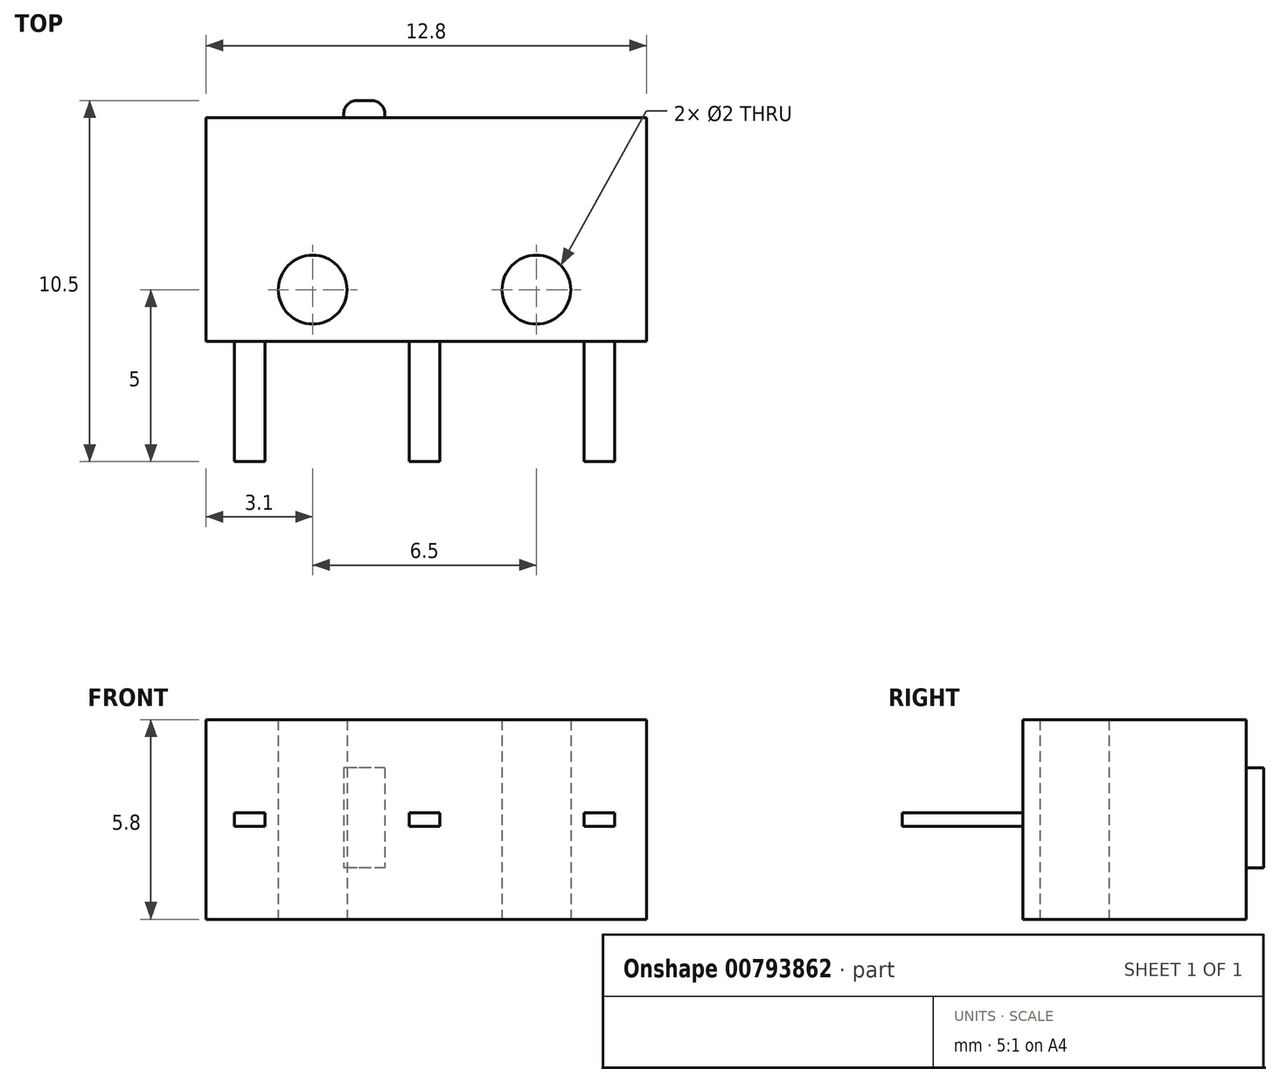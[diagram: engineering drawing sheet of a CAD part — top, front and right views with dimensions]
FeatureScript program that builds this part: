
annotation { "Feature Type Name" : "Feature", "Feature Type Description" : "" }
export const myFeature = defineFeature(function(context is Context, id is Id, definition is map)
    precondition{}
    {
        {
            var Q0;
            Q0=qCreatedBy(makeId("Top.planeOp"),FACE);
            var sketch = newSketch(context, id + "F0", { "sketchPlane" : qUnion([Q0])});
            skLineSegment(sketch, "E0.bottom", {"start": v(-6.35, 3.25) * mm, "end": v(6.45, 3.25) * mm});
            skLineSegment(sketch, "E0.top", {"start": v(-6.35, -3.25) * mm, "end": v(6.45, -3.25) * mm});
            skLineSegment(sketch, "E0.left", {"start": v(-6.35, 3.25) * mm, "end": v(-6.35, -3.25) * mm});
            skLineSegment(sketch, "E0.right", {"start": v(6.45, 3.25) * mm, "end": v(6.45, -3.25) * mm});
            skCircle(sketch, "E1", {"center": v(-3.25, -1.75) * mm, "radius": 1 * mm});
            skCircle(sketch, "E2", {"center": v(3.25, -1.75) * mm, "radius": 1 * mm});
            skSolve(sketch);
        }
        {
            var Q0;
            Q0=qSketchRegion(id+"F0",true);
            extrude(context, id + "F1", {"entities" : qUnion([Q0]), "depth" : 5.8 * mm, "offsetDistance" : 25 * mm});
        }
        {
            var Q0;
            Q0=makeQuery(id+"F1.opExtrude","SWEPT_FACE",FACE,{"disambiguationData":[OSD([sQuery(id+"F0.wireOp",EDGE,"E0.bottom")])]});
            var sketch = newSketch(context, id + "F2", { "sketchPlane" : qUnion([Q0])});
            skLineSegment(sketch, "E3.bottom", {"start": v(1.15, 4.4) * mm, "end": v(2.35, 4.4) * mm});
            skLineSegment(sketch, "E3.top", {"start": v(1.15, 1.5) * mm, "end": v(2.35, 1.5) * mm});
            skLineSegment(sketch, "E3.left", {"start": v(1.15, 4.4) * mm, "end": v(1.15, 1.5) * mm});
            skLineSegment(sketch, "E3.right", {"start": v(2.35, 4.4) * mm, "end": v(2.35, 1.5) * mm});
            skLineSegment(sketch, "E4", {"start": v(-3.25, 5.8) * mm, "end": v(-3.25, 0) * mm, "construction": true});
            skSolve(sketch);
        }
        {
            var Q0;
            Q0=qCreatedBy(makeId("Top.planeOp"),FACE);
            cPlane(context, id + "F3", {"entities" : qUnion([Q0]), "cplaneType" : CPlaneType.OFFSET, "offset" : 2.7 * mm, "width" : 150 * mm, "height" : 150 * mm});
        }
        {
            var Q0;
            Q0=qCreatedBy(id+"F3.planeOp",FACE);
            var sketch = newSketch(context, id + "F4", { "sketchPlane" : qUnion([Q0])});
            skLineSegment(sketch, "E5.bottom", {"start": v(-5.53, -3.25) * mm, "end": v(-4.63, -3.25) * mm});
            skLineSegment(sketch, "E5.top", {"start": v(-5.53, -6.75) * mm, "end": v(-4.63, -6.75) * mm});
            skLineSegment(sketch, "E5.left", {"start": v(-5.53, -3.25) * mm, "end": v(-5.53, -6.75) * mm});
            skLineSegment(sketch, "E5.right", {"start": v(-4.63, -3.25) * mm, "end": v(-4.63, -6.75) * mm});
            skLineSegment(sketch, "E6.bottom", {"start": v(-0.45, -3.25) * mm, "end": v(0.45, -3.25) * mm});
            skLineSegment(sketch, "E6.top", {"start": v(-0.45, -6.75) * mm, "end": v(0.45, -6.75) * mm});
            skLineSegment(sketch, "E6.left", {"start": v(-0.45, -3.25) * mm, "end": v(-0.45, -6.75) * mm});
            skLineSegment(sketch, "E6.right", {"start": v(0.45, -3.25) * mm, "end": v(0.45, -6.75) * mm});
            skLineSegment(sketch, "E7.bottom", {"start": v(4.63, -3.25) * mm, "end": v(5.53, -3.25) * mm});
            skLineSegment(sketch, "E7.top", {"start": v(4.63, -6.75) * mm, "end": v(5.53, -6.75) * mm});
            skLineSegment(sketch, "E7.left", {"start": v(4.63, -3.25) * mm, "end": v(4.63, -6.75) * mm});
            skLineSegment(sketch, "E7.right", {"start": v(5.53, -3.25) * mm, "end": v(5.53, -6.75) * mm});
            skPoint(sketch, "E8", {"position": v(-5.08, -6.75) * mm});
            skPoint(sketch, "E9", {"position": v(5.08, -6.75) * mm});
            skSolve(sketch);
        }
        {
            var Q0;
            Q0=qSketchRegion(id+"F4",true);
            extrude(context, id + "F5", {"entities" : qUnion([Q0]), "operationType" : NewBodyOperationType.ADD, "depth" : 0.4 * mm});
        }
        {
            var Q0;
            Q0=qSketchRegion(id+"F2",true);
            extrude(context, id + "F6", {"entities" : qUnion([Q0]), "operationType" : NewBodyOperationType.ADD, "depth" : .5 * mm});
        }
        {
            var Q0;
            Q0=makeQuery(id+"F6.opExtrude","CAP_EDGE",EDGE,{"disambiguationData":[OSD([sQuery(id+"F2.wireOp",EDGE,"E3.right")])],"isStart":false});
            var Q1;
            Q1=makeQuery(id+"F6.opExtrude","CAP_EDGE",EDGE,{"disambiguationData":[OSD([sQuery(id+"F2.wireOp",EDGE,"E3.left")])],"isStart":false});
            fillet(context, id + "F7", {"entities" : qUnion([Q0, Q1]), "radius" : .4 * mm, "tangentPropagation" : true, "allowEdgeOverflow" : false});
        }
    });
